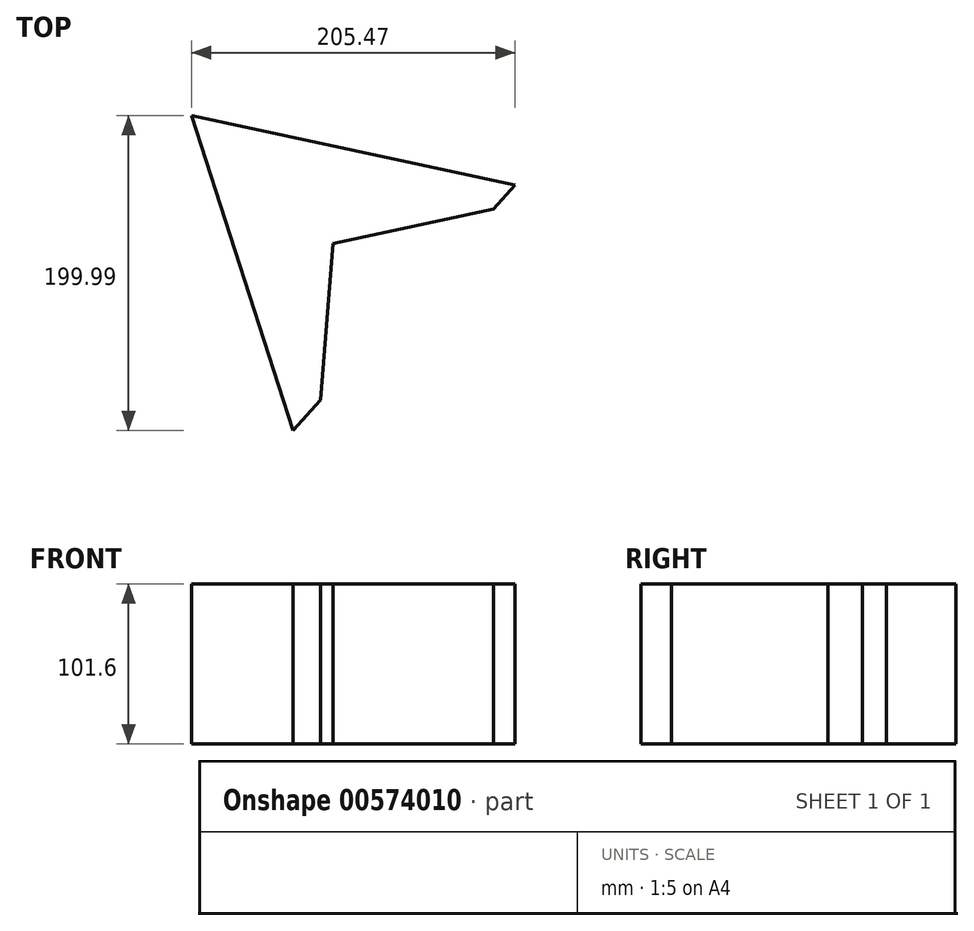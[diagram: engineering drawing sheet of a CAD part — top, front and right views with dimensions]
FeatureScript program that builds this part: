
annotation { "Feature Type Name" : "Feature", "Feature Type Description" : "" }
export const myFeature = defineFeature(function(context is Context, id is Id, definition is map)
    precondition{}
    {
        {
            var Q0;
            Q0=qCreatedBy(makeId("Top.planeOp"),FACE);
            var sketch = newSketch(context, id + "F0", { "sketchPlane" : qUnion([Q0])});
            skCircle(sketch, "E0.cCircle", {"center": v(0, 0) * mm, "radius": 60.66 * mm, "construction": true});
            skLineSegment(sketch, "E0.0", {"start": v(115.46, 37.27) * mm, "end": v(-25.45, -118.63) * mm});
            skLineSegment(sketch, "E0.1", {"start": v(-25.45, -118.63) * mm, "end": v(-90, 81.36) * mm});
            skLineSegment(sketch, "E0.2", {"start": v(-90, 81.36) * mm, "end": v(115.46, 37.27) * mm});
            skPoint(sketch, "E0.0.midPoint", {"position": v(45, -40.68) * mm});
            skArc(sketch, "E1", {"start": v(0, 0) * mm, "mid": v(-34.62, 0.09) * mm, "end": v(-53.22, -29.11) * mm});
            skArc(sketch, "E2", {"start": v(41.79, 53.08) * mm, "mid": v(6.83, 37.61) * mm, "end": v(0, 0) * mm});
            skLineSegment(sketch, "E3", {"start": v(0, 0) * mm, "end": v(-8.04, -99.37) * mm});
            skLineSegment(sketch, "E4", {"start": v(0, 0) * mm, "end": v(101.63, 21.97) * mm});
            skLineSegment(sketch, "E5", {"start": v(0, 0) * mm, "end": v(-53.22, -29.11) * mm});
            skLineSegment(sketch, "E6", {"start": v(0, 0) * mm, "end": v(41.79, 53.08) * mm});
            skLineSegment(sketch, "E7", {"start": v(-53.22, -29.11) * mm, "end": v(-57.73, 74.43) * mm});
            skPoint(sketch, "E7.endSnap0", {"position": v(-57.73, -18.64) * mm});
            skLineSegment(sketch, "E8", {"start": v(41.79, 53.08) * mm, "end": v(-80.88, 53.08) * mm});
            skLineSegment(sketch, "E9", {"start": v(0, 0) * mm, "end": v(-56.8, 53.08) * mm});
            skSolve(sketch);
        }
        {
            var Q0;
            {var subQ0=sQuery(id+"F0.wireOp",EDGE,"E0.2");var subQ1=sQuery(id+"F0.wireOp",EDGE,"E0.1");var subQ2=makeQuery(id+"F0.imprint","INTERSECT",VERTEX,{"derivedFrom":[subQ1,subQ0]});Q0=makeQuery(id+"F0.imprint","IMPRINT",FACE,{"disambiguationData":[TD([[makeQuery(id+"F0.imprint","IMPRINT",EDGE,{"disambiguationData":[TD([[subQ2,1.0]])],"derivedFrom":subQ1}),-1.0]])]});}
            var Q1;
            {var subQ0=sQuery(id+"F0.wireOp",EDGE,"E8");var subQ1=sQuery(id+"F0.wireOp",EDGE,"E2");var subQ3=makeQuery(id+"F0.imprint","INTERSECT",VERTEX,{"derivedFrom":[subQ1,subQ0]});Q1=makeQuery(id+"F0.imprint","IMPRINT",FACE,{"disambiguationData":[TD([[makeQuery(id+"F0.imprint","IMPRINT",EDGE,{"disambiguationData":[TD([[subQ3,1.0]])],"derivedFrom":subQ1}),1.0]])]});}
            var Q2;
            {var subQ2=sQuery(id+"F0.wireOp",EDGE,"E0.2");var subQ4=sQuery(id+"F0.wireOp",EDGE,"E7");var subQ5=makeQuery(id+"F0.imprint","INTERSECT",VERTEX,{"derivedFrom":[subQ2,subQ4]});Q2=makeQuery(id+"F0.imprint","IMPRINT",FACE,{"disambiguationData":[TD([[makeQuery(id+"F0.imprint","IMPRINT",EDGE,{"disambiguationData":[TD([[subQ5,1.0]])],"derivedFrom":subQ4}),-1.0]])]});}
            var Q3;
            {var subQ0=sQuery(id+"F0.wireOp",EDGE,"E6");Q3=makeQuery(id+"F0.imprint","IMPRINT",FACE,{"disambiguationData":[TD([[makeQuery(id+"F0.imprint","IMPRINT",EDGE,{"derivedFrom":subQ0}),1.0]])]});}
            var Q4;
            Q4=makeQuery(id+"F0.imprint","IMPRINT",FACE,{"disambiguationData":[TD([[makeQuery(id+"F0.imprint","IMPRINT",EDGE,{"derivedFrom":sQuery(id+"F0.wireOp",EDGE,"E1")}),1.0]])]});
            var Q5;
            {var subQ3=sQuery(id+"F0.wireOp",EDGE,"E4");Q5=makeQuery(id+"F0.imprint","IMPRINT",FACE,{"disambiguationData":[TD([[makeQuery(id+"F0.imprint","IMPRINT",EDGE,{"derivedFrom":subQ3}),1.0]])]});}
            var Q6;
            {var subQ0=sQuery(id+"F0.wireOp",EDGE,"E3");Q6=makeQuery(id+"F0.imprint","IMPRINT",FACE,{"disambiguationData":[TD([[makeQuery(id+"F0.imprint","IMPRINT",EDGE,{"derivedFrom":subQ0}),-1.0]])]});}
            var Q7;
            {var subQ0=sQuery(id+"F0.wireOp",EDGE,"E1");Q7=makeQuery(id+"F0.imprint","IMPRINT",FACE,{"disambiguationData":[TD([[makeQuery(id+"F0.imprint","IMPRINT",EDGE,{"derivedFrom":subQ0}),-1.0]])]});}
            var Q8;
            {var subQ0=sQuery(id+"F0.wireOp",EDGE,"E9");Q8=makeQuery(id+"F0.imprint","IMPRINT",FACE,{"disambiguationData":[TD([[makeQuery(id+"F0.imprint","IMPRINT",EDGE,{"derivedFrom":subQ0}),-1.0]])]});}
            extrude(context, id + "F1", {"entities" : qUnion([Q0, Q1, Q2, Q3, Q4, Q5, Q6, Q7, Q8]), "depth" : 101.6 * mm, "offsetDistance" : 25.4 * mm});
        }
    });
